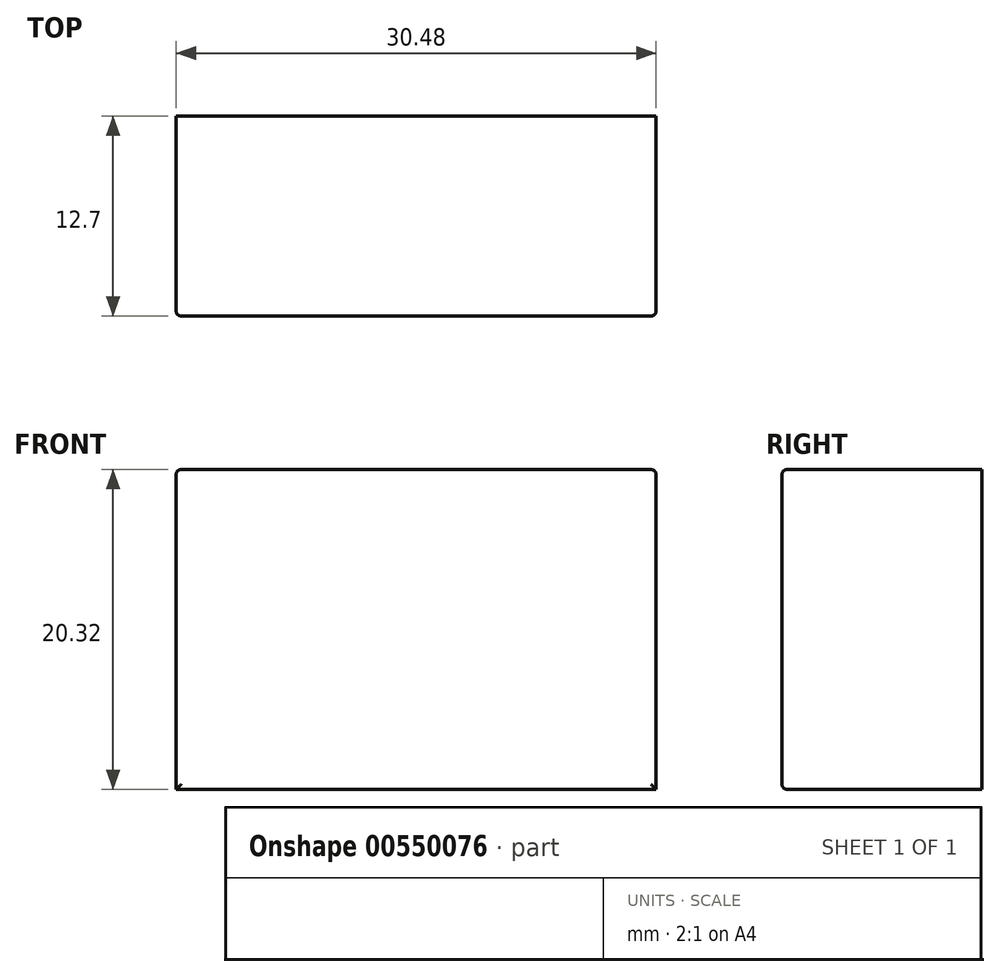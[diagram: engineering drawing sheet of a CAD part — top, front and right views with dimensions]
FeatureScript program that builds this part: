
annotation { "Feature Type Name" : "Feature", "Feature Type Description" : "" }
export const myFeature = defineFeature(function(context is Context, id is Id, definition is map)
    precondition{}
    {
        {
            var Q0;
            Q0=qCreatedBy(makeId("Top.planeOp"),FACE);
            var sketch = newSketch(context, id + "F0", { "sketchPlane" : qUnion([Q0])});
            skLineSegment(sketch, "E0.bottom", {"start": v(15.24, 6.35) * mm, "end": v(-15.24, 6.35) * mm});
            skLineSegment(sketch, "E0.top", {"start": v(15.24, -6.35) * mm, "end": v(-15.24, -6.35) * mm});
            skLineSegment(sketch, "E0.left", {"start": v(15.24, 6.35) * mm, "end": v(15.24, -6.35) * mm});
            skLineSegment(sketch, "E0.right", {"start": v(-15.24, 6.35) * mm, "end": v(-15.24, -6.35) * mm});
            skPoint(sketch, "E0.middle", {"position": v(0, 0) * mm});
            skSolve(sketch);
        }
        {
            var Q0;
            Q0=makeQuery(id+"F0.imprint","IMPRINT",FACE,{"disambiguationData":[TD([[makeQuery(id+"F0.imprint","IMPRINT",EDGE,{"derivedFrom":sQuery(id+"F0.wireOp",EDGE,"E0.bottom")}),1.0]])]});
            extrude(context, id + "F1", {"entities" : qUnion([Q0]), "oppositeDirection" : true, "depth" : 20.32 * mm, "offsetDistance" : 25.4 * mm});
        }
        {
            var Q0;
            Q0=makeQuery(id+"F1.opExtrude","CAP_EDGE",EDGE,{"disambiguationData":[OSD([sQuery(id+"F0.wireOp",EDGE,"E0.left")])],"isStart":true});
            var Q1;
            Q1=makeQuery(id+"F1.opExtrude","CAP_EDGE",EDGE,{"disambiguationData":[OSD([sQuery(id+"F0.wireOp",EDGE,"E0.top")])],"isStart":true});
            var Q2;
            Q2=makeQuery(id+"F1.opExtrude","CAP_EDGE",EDGE,{"disambiguationData":[OSD([sQuery(id+"F0.wireOp",EDGE,"E0.right")])],"isStart":true});
            var Q3;
            Q3=makeQuery(id+"F1.opExtrude","SWEPT_EDGE",EDGE,{"disambiguationData":[OSD([sQuery(id+"F0.wireOp",EDGE,"E0.top"),sQuery(id+"F0.wireOp",EDGE,"E0.left")])]});
            var Q4;
            Q4=makeQuery(id+"F1.opExtrude","CAP_EDGE",EDGE,{"disambiguationData":[OSD([sQuery(id+"F0.wireOp",EDGE,"E0.top")])],"isStart":false});
            var Q5;
            Q5=makeQuery(id+"F1.opExtrude","SWEPT_EDGE",EDGE,{"disambiguationData":[OSD([sQuery(id+"F0.wireOp",EDGE,"E0.top"),sQuery(id+"F0.wireOp",EDGE,"E0.right")])]});
            fillet(context, id + "F2", {"entities" : qUnion([Q0, Q1, Q2, Q3, Q4, Q5]), "radius" : 0.32 * mm, "tangentPropagation" : true, "allowEdgeOverflow" : false});
        }
    });
